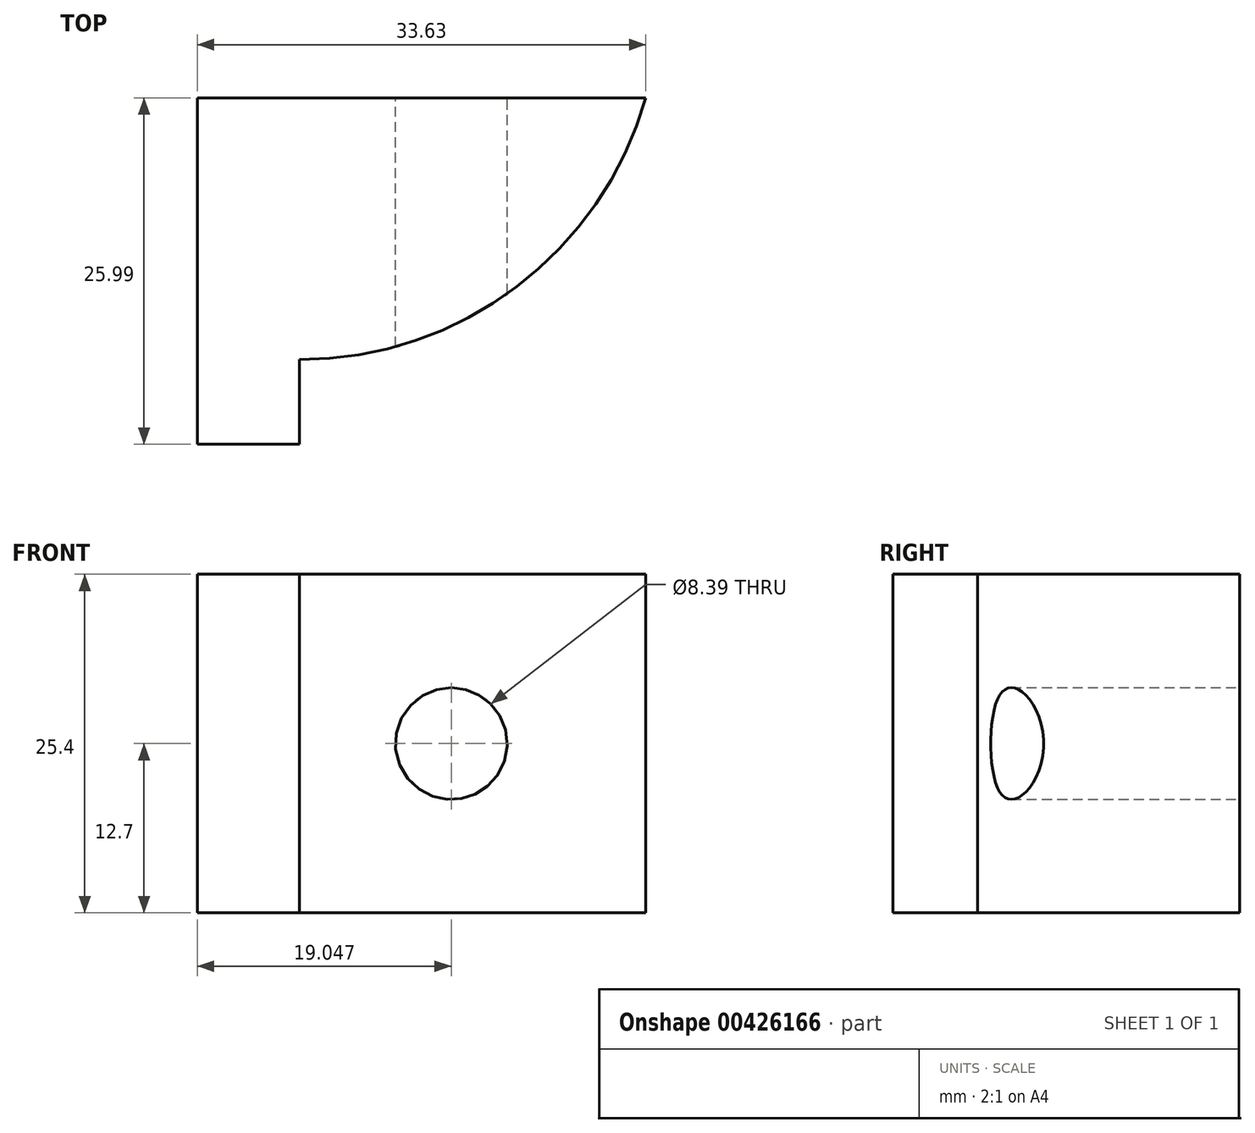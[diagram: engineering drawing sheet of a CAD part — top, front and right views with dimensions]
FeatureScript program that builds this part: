
annotation { "Feature Type Name" : "Feature", "Feature Type Description" : "" }
export const myFeature = defineFeature(function(context is Context, id is Id, definition is map)
    precondition{}
    {
        {
            var Q0;
            Q0=qCreatedBy(makeId("Top.planeOp"),FACE);
            var sketch = newSketch(context, id + "F0", { "sketchPlane" : qUnion([Q0])});
            skLineSegment(sketch, "E0.bottom", {"start": v(-33.63, 19.64) * mm, "end": v(0, 19.64) * mm});
            skLineSegment(sketch, "E0.top", {"start": v(-33.63, 0) * mm, "end": v(0, 0) * mm});
            skLineSegment(sketch, "E0.left", {"start": v(-33.63, 19.64) * mm, "end": v(-33.63, 0) * mm});
            skLineSegment(sketch, "E0.right", {"start": v(0, 19.64) * mm, "end": v(0, 0) * mm});
            skSolve(sketch);
        }
        {
            var Q0;
            Q0=makeQuery(id+"F0.imprint","IMPRINT",FACE,{"disambiguationData":[TD([[makeQuery(id+"F0.imprint","IMPRINT",EDGE,{"derivedFrom":sQuery(id+"F0.wireOp",EDGE,"E0.bottom")}),-1.0]])]});
            extrude(context, id + "F1", {"entities" : qUnion([Q0]), "depth" : 25.4 * mm});
        }
        {
            var Q0;
            Q0=makeQuery(id+"F1.opExtrude","SWEPT_EDGE",EDGE,{"disambiguationData":[OSD([sQuery(id+"F0.wireOp",EDGE,"E0.top"),sQuery(id+"F0.wireOp",EDGE,"E0.right")])]});
            fillet(context, id + "F2", {"entities" : qUnion([Q0]), "radius" : 26.98 * mm, "tangentPropagation" : true, "allowEdgeOverflow" : false});
        }
        {
            var Q0;
            Q0=makeQuery(id+"F1.opExtrude","SWEPT_FACE",FACE,{"disambiguationData":[OSD([sQuery(id+"F0.wireOp",EDGE,"E0.bottom")])]});
            var sketch = newSketch(context, id + "F3", { "sketchPlane" : qUnion([Q0])});
            skCircle(sketch, "E1", {"center": v(14.58, 12.7) * mm, "radius": 4.2 * mm});
            skSolve(sketch);
        }
        {
            var Q0;
            Q0=makeQuery(id+"F3.imprint","IMPRINT",FACE,{"disambiguationData":[TD([[makeQuery(id+"F3.imprint","IMPRINT",EDGE,{"derivedFrom":sQuery(id+"F3.wireOp",EDGE,"E1")}),1.0]])]});
            extrude(context, id + "F4", {"entities" : qUnion([Q0]), "operationType" : NewBodyOperationType.REMOVE, "oppositeDirection" : true, "depth" : 41.4 * mm});
        }
        {
            var Q0;
            Q0=makeQuery(id+"F1.opExtrude","SWEPT_FACE",FACE,{"disambiguationData":[OSD([sQuery(id+"F0.wireOp",EDGE,"E0.top")])]});
            extrude(context, id + "F5", {"entities" : qUnion([Q0]), "operationType" : NewBodyOperationType.ADD, "depth" : 6.35 * mm});
        }
    });
